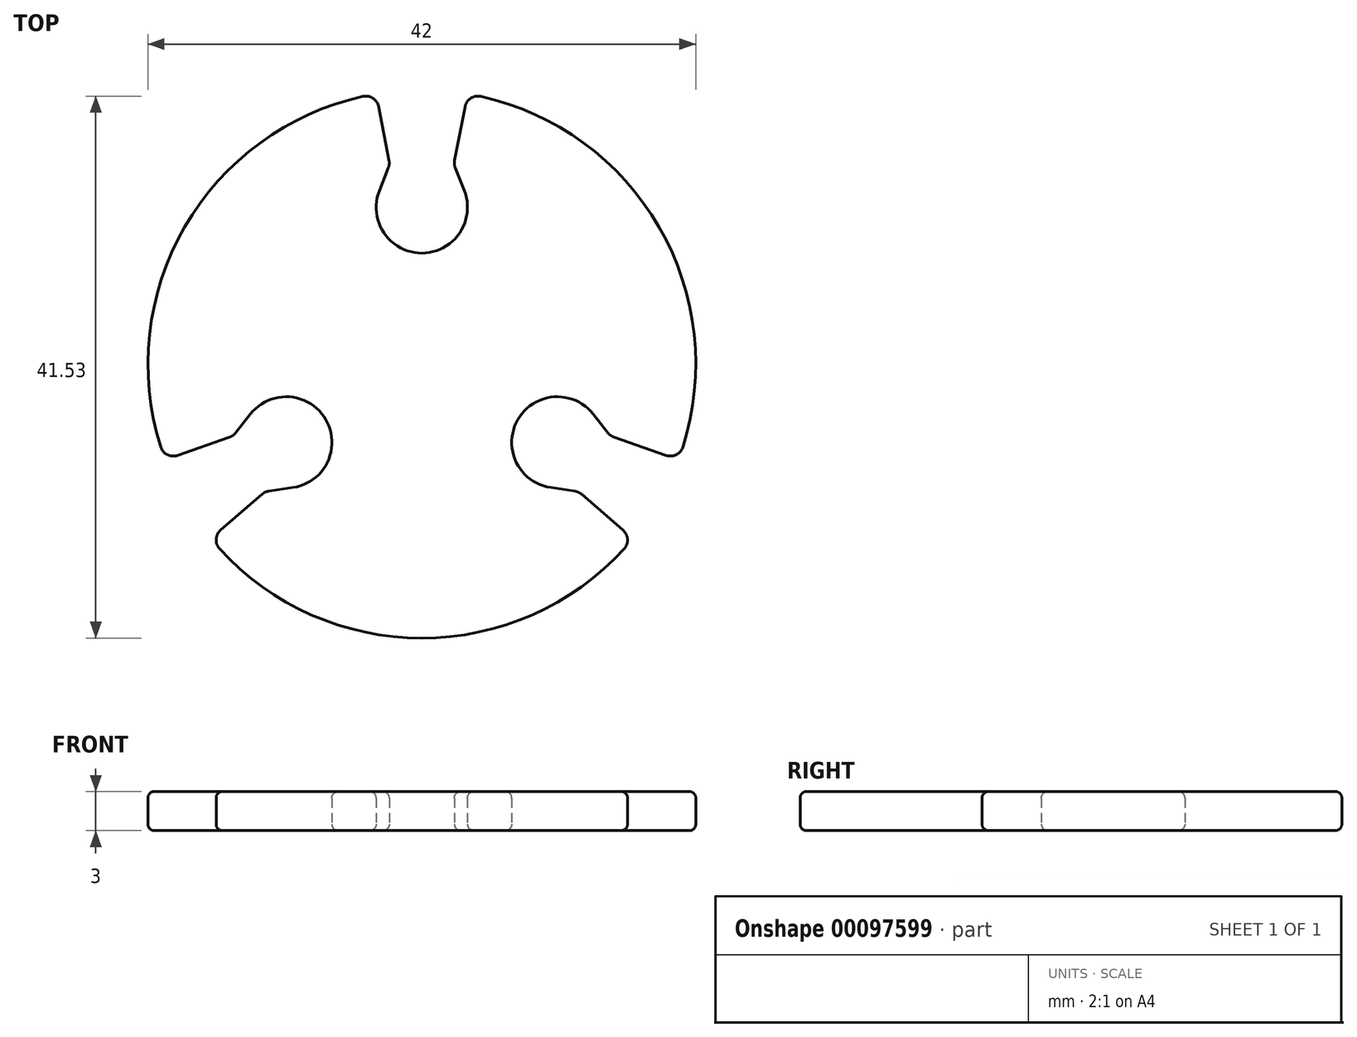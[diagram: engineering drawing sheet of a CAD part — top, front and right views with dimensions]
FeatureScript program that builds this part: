
annotation { "Feature Type Name" : "Feature", "Feature Type Description" : "" }
export const myFeature = defineFeature(function(context is Context, id is Id, definition is map)
    precondition{}
    {
        {
            var Q0;
            Q0=qCreatedBy(makeId("Top.planeOp"),FACE);
            var sketch = newSketch(context, id + "F0", { "sketchPlane" : qUnion([Q0])});
            skLineSegment(sketch, "E0", {"start": v(0, 0) * mm, "end": v(0, 21) * mm, "construction": true});
            skArc(sketch, "E1", {"start": v(-3.25, 13.3) * mm, "mid": v(0, 8.5) * mm, "end": v(3.25, 13.3) * mm});
            skLineSegment(sketch, "E2", {"start": v(-2.57, 15.02) * mm, "end": v(-3.25, 13.3) * mm});
            skLineSegment(sketch, "E3", {"start": v(-3.5, 12) * mm, "end": v(-3.5, 20.7) * mm, "construction": true});
            skLineSegment(sketch, "E4.0", {"start": v(-2.5, 0) * mm, "end": v(-2.5, 21) * mm, "construction": true});
            skLineSegment(sketch, "E5", {"start": v(-2.51, 15.58) * mm, "end": v(-3.31, 19.72) * mm});
            skLineSegment(sketch, "E6.MirrorCS", {"start": v(2.52, 15.59) * mm, "end": v(3.31, 19.72) * mm});
            skLineSegment(sketch, "E7.MirrorCS", {"start": v(2.57, 15.03) * mm, "end": v(3.25, 13.3) * mm});
            skPoint(sketch, "E8.visualSharp", {"position": v(-2.5, 15.3) * mm});
            skArc(sketch, "E8.filletArc", {"start": v(-2.57, 15.02) * mm, "mid": v(-2.5, 15.3) * mm, "end": v(-2.51, 15.58) * mm});
            skPoint(sketch, "E9.visualSharp", {"position": v(2.46, 15.3) * mm});
            skArc(sketch, "E9.filletArc", {"start": v(2.52, 15.59) * mm, "mid": v(2.5, 15.3) * mm, "end": v(2.57, 15.03) * mm});
            skArc(sketch, "E10.1.3", {"start": v(-15.59, 2.52) * mm, "mid": v(-15.3, 2.5) * mm, "end": v(-15.03, 2.57) * mm});
            skArc(sketch, "E10.1.4", {"start": v(-15.02, -2.57) * mm, "mid": v(-15.3, -2.5) * mm, "end": v(-15.58, -2.51) * mm});
            skPoint(sketch, "E10.center", {"position": v(0, 0) * mm});
            skPoint(sketch, "E11.visualSharp", {"position": v(-20.7, 3.5) * mm});
            skPoint(sketch, "E12.visualSharp", {"position": v(-20.7, -3.5) * mm});
            skPoint(sketch, "E13.visualSharp", {"position": v(-3.5, 20.7) * mm});
            skArc(sketch, "E13.filletArc", {"start": v(-3.31, 19.72) * mm, "mid": v(-3.74, 20.37) * mm, "end": v(-4.5, 20.51) * mm});
            skPoint(sketch, "E14.visualSharp", {"position": v(3.5, 20.7) * mm});
            skArc(sketch, "E14.filletArc", {"start": v(4.5, 20.51) * mm, "mid": v(3.74, 20.37) * mm, "end": v(3.31, 19.72) * mm});
            skCircle(sketch, "E15", {"center": v(0, 0) * mm, "radius": 15.5 * mm, "construction": true});
            skArc(sketch, "E16.1.0", {"start": v(-15.43, -12.73) * mm, "mid": v(-15.77, -13.43) * mm, "end": v(-15.5, -14.16) * mm});
            skLineSegment(sketch, "E16.1.1", {"start": v(-12.24, -9.97) * mm, "end": v(-15.43, -12.73) * mm});
            skLineSegment(sketch, "E16.1.2", {"start": v(-11.73, -9.73) * mm, "end": v(-9.88, -9.46) * mm});
            skArc(sketch, "E16.1.3", {"start": v(-9.88, -9.46) * mm, "mid": v(-7.36, -4.25) * mm, "end": v(-13.14, -3.83) * mm});
            skLineSegment(sketch, "E16.1.4", {"start": v(-14.3, -5.3) * mm, "end": v(-13.14, -3.83) * mm});
            skArc(sketch, "E16.1.5", {"start": v(-14.76, -5.62) * mm, "mid": v(-14.5, -5.49) * mm, "end": v(-14.3, -5.3) * mm});
            skArc(sketch, "E16.1.6", {"start": v(-11.73, -9.73) * mm, "mid": v(-12, -9.81) * mm, "end": v(-12.24, -9.97) * mm});
            skLineSegment(sketch, "E16.1.7", {"start": v(-14.76, -5.62) * mm, "end": v(-18.74, -7) * mm});
            skArc(sketch, "E16.1.8", {"start": v(-20.02, -6.35) * mm, "mid": v(-19.51, -6.94) * mm, "end": v(-18.74, -7) * mm});
            skArc(sketch, "E16.2.0", {"start": v(18.74, -7) * mm, "mid": v(19.51, -6.94) * mm, "end": v(20.02, -6.35) * mm});
            skLineSegment(sketch, "E16.2.1", {"start": v(14.75, -5.61) * mm, "end": v(18.74, -7) * mm});
            skLineSegment(sketch, "E16.2.2", {"start": v(14.3, -5.29) * mm, "end": v(13.14, -3.83) * mm});
            skArc(sketch, "E16.2.3", {"start": v(13.14, -3.83) * mm, "mid": v(7.36, -4.25) * mm, "end": v(9.88, -9.46) * mm});
            skLineSegment(sketch, "E16.2.4", {"start": v(11.74, -9.74) * mm, "end": v(9.88, -9.46) * mm});
            skArc(sketch, "E16.2.5", {"start": v(12.24, -9.97) * mm, "mid": v(12, -9.82) * mm, "end": v(11.74, -9.74) * mm});
            skArc(sketch, "E16.2.6", {"start": v(14.3, -5.29) * mm, "mid": v(14.5, -5.48) * mm, "end": v(14.75, -5.61) * mm});
            skLineSegment(sketch, "E16.2.7", {"start": v(12.24, -9.97) * mm, "end": v(15.43, -12.73) * mm});
            skArc(sketch, "E16.2.8", {"start": v(15.5, -14.16) * mm, "mid": v(15.77, -13.43) * mm, "end": v(15.43, -12.73) * mm});
            skArc(sketch, "E17", {"start": v(-15.5, -14.16) * mm, "mid": v(0, -21) * mm, "end": v(15.5, -14.16) * mm});
            skArc(sketch, "E18.trimOffspring", {"start": v(20.02, -6.35) * mm, "mid": v(18.19, 10.5) * mm, "end": v(4.5, 20.51) * mm});
            skArc(sketch, "E19.trimOffspring", {"start": v(-4.5, 20.51) * mm, "mid": v(-18.19, 10.5) * mm, "end": v(-20.02, -6.35) * mm});
            skSolve(sketch);
        }
        {
            var Q0;
            Q0 = qSketchRegion(id + "F0", true);
            extrude(context, id + "F1", {"entities" : qUnion([Q0]), "depth" : 3 * mm, "offsetDistance" : 25 * mm});
        }
        {
            var Q0;
            Q0=makeQuery(id+"F1.opExtrude","CAP_FACE",FACE,{"disambiguationData":[OSD([sQuery(id+"F0.wireOp",EDGE,"4tVSPkAX-6ott-23qE-Cy5R-RKtk7fITxtp3"),sQuery(id+"F0.wireOp",EDGE,"E1"),sQuery(id+"F0.wireOp",EDGE,"E2"),sQuery(id+"F0.wireOp",EDGE,"E5"),sQuery(id+"F0.wireOp",EDGE,"E6.MirrorCS"),sQuery(id+"F0.wireOp",EDGE,"E7.MirrorCS"),sQuery(id+"F0.wireOp",EDGE,"E8.filletArc"),sQuery(id+"F0.wireOp",EDGE,"E9.filletArc"),sQuery(id+"F0.wireOp",EDGE,"E10.1.0"),sQuery(id+"F0.wireOp",EDGE,"E10.1.1"),sQuery(id+"F0.wireOp",EDGE,"E10.1.2"),sQuery(id+"F0.wireOp",EDGE,"E10.1.3"),sQuery(id+"F0.wireOp",EDGE,"E10.1.4"),sQuery(id+"F0.wireOp",EDGE,"E10.1.5"),sQuery(id+"F0.wireOp",EDGE,"E10.1.6"),sQuery(id+"F0.wireOp",EDGE,"E10.2.0"),sQuery(id+"F0.wireOp",EDGE,"E10.2.1"),sQuery(id+"F0.wireOp",EDGE,"E10.2.2"),sQuery(id+"F0.wireOp",EDGE,"E10.2.3"),sQuery(id+"F0.wireOp",EDGE,"E10.2.4"),sQuery(id+"F0.wireOp",EDGE,"E10.2.5"),sQuery(id+"F0.wireOp",EDGE,"E10.2.6"),sQuery(id+"F0.wireOp",EDGE,"E10.3.0"),sQuery(id+"F0.wireOp",EDGE,"E10.3.1"),sQuery(id+"F0.wireOp",EDGE,"E10.3.2"),sQuery(id+"F0.wireOp",EDGE,"E10.3.3"),sQuery(id+"F0.wireOp",EDGE,"E10.3.4"),sQuery(id+"F0.wireOp",EDGE,"E10.3.5"),sQuery(id+"F0.wireOp",EDGE,"E10.3.6"),sQuery(id+"F0.wireOp",EDGE,"e0651744-e2f5-44a9-b1f0-2c6e2f3295b8.trimOffspring"),sQuery(id+"F0.wireOp",EDGE,"c18df3e6-d1d7-4a62-a432-acc3b0751ca2.trimOffspring"),sQuery(id+"F0.wireOp",EDGE,"67d30ffb-87cf-4c86-a316-4f6115b99f8b.trimOffspring"),sQuery(id+"F0.wireOp",EDGE,"E11.filletArc"),sQuery(id+"F0.wireOp",EDGE,"E12.filletArc"),sQuery(id+"F0.wireOp",EDGE,"E13.filletArc"),sQuery(id+"F0.wireOp",EDGE,"E14.filletArc"),sQuery(id+"F0.wireOp",EDGE,"7c52f6a3-9a07-4745-9d79-d9e1ef602308.filletArc"),sQuery(id+"F0.wireOp",EDGE,"73534b26-475d-4137-9a86-ba68f8b524e3.filletArc"),sQuery(id+"F0.wireOp",EDGE,"5c68d350-ee31-40ce-a193-baf9a7cb5b4c.filletArc"),sQuery(id+"F0.wireOp",EDGE,"f3d94749-2a68-4ce9-8eb8-13c5c79f92ef.filletArc")])],"isStart":false});
            var Q1;
            Q1=makeQuery(id+"F1.opExtrude","CAP_FACE",FACE,{"disambiguationData":[OSD([sQuery(id+"F0.wireOp",EDGE,"4tVSPkAX-6ott-23qE-Cy5R-RKtk7fITxtp3"),sQuery(id+"F0.wireOp",EDGE,"E1"),sQuery(id+"F0.wireOp",EDGE,"E2"),sQuery(id+"F0.wireOp",EDGE,"E5"),sQuery(id+"F0.wireOp",EDGE,"E6.MirrorCS"),sQuery(id+"F0.wireOp",EDGE,"E7.MirrorCS"),sQuery(id+"F0.wireOp",EDGE,"E8.filletArc"),sQuery(id+"F0.wireOp",EDGE,"E9.filletArc"),sQuery(id+"F0.wireOp",EDGE,"E10.1.0"),sQuery(id+"F0.wireOp",EDGE,"E10.1.1"),sQuery(id+"F0.wireOp",EDGE,"E10.1.2"),sQuery(id+"F0.wireOp",EDGE,"E10.1.3"),sQuery(id+"F0.wireOp",EDGE,"E10.1.4"),sQuery(id+"F0.wireOp",EDGE,"E10.1.5"),sQuery(id+"F0.wireOp",EDGE,"E10.1.6"),sQuery(id+"F0.wireOp",EDGE,"E10.2.0"),sQuery(id+"F0.wireOp",EDGE,"E10.2.1"),sQuery(id+"F0.wireOp",EDGE,"E10.2.2"),sQuery(id+"F0.wireOp",EDGE,"E10.2.3"),sQuery(id+"F0.wireOp",EDGE,"E10.2.4"),sQuery(id+"F0.wireOp",EDGE,"E10.2.5"),sQuery(id+"F0.wireOp",EDGE,"E10.2.6"),sQuery(id+"F0.wireOp",EDGE,"E10.3.0"),sQuery(id+"F0.wireOp",EDGE,"E10.3.1"),sQuery(id+"F0.wireOp",EDGE,"E10.3.2"),sQuery(id+"F0.wireOp",EDGE,"E10.3.3"),sQuery(id+"F0.wireOp",EDGE,"E10.3.4"),sQuery(id+"F0.wireOp",EDGE,"E10.3.5"),sQuery(id+"F0.wireOp",EDGE,"E10.3.6"),sQuery(id+"F0.wireOp",EDGE,"e0651744-e2f5-44a9-b1f0-2c6e2f3295b8.trimOffspring"),sQuery(id+"F0.wireOp",EDGE,"c18df3e6-d1d7-4a62-a432-acc3b0751ca2.trimOffspring"),sQuery(id+"F0.wireOp",EDGE,"67d30ffb-87cf-4c86-a316-4f6115b99f8b.trimOffspring"),sQuery(id+"F0.wireOp",EDGE,"E11.filletArc"),sQuery(id+"F0.wireOp",EDGE,"E12.filletArc"),sQuery(id+"F0.wireOp",EDGE,"E13.filletArc"),sQuery(id+"F0.wireOp",EDGE,"E14.filletArc"),sQuery(id+"F0.wireOp",EDGE,"7c52f6a3-9a07-4745-9d79-d9e1ef602308.filletArc"),sQuery(id+"F0.wireOp",EDGE,"73534b26-475d-4137-9a86-ba68f8b524e3.filletArc"),sQuery(id+"F0.wireOp",EDGE,"5c68d350-ee31-40ce-a193-baf9a7cb5b4c.filletArc"),sQuery(id+"F0.wireOp",EDGE,"f3d94749-2a68-4ce9-8eb8-13c5c79f92ef.filletArc")])],"isStart":true});
            fillet(context, id + "F2", {"entities" : qUnion([Q0, Q1]), "tangentPropagation" : true, "radius" : 0.5 * mm, "defaultsChanged" : false, "vertexSettings" : [], "allowEdgeOverflow" : false});
        }
    });
